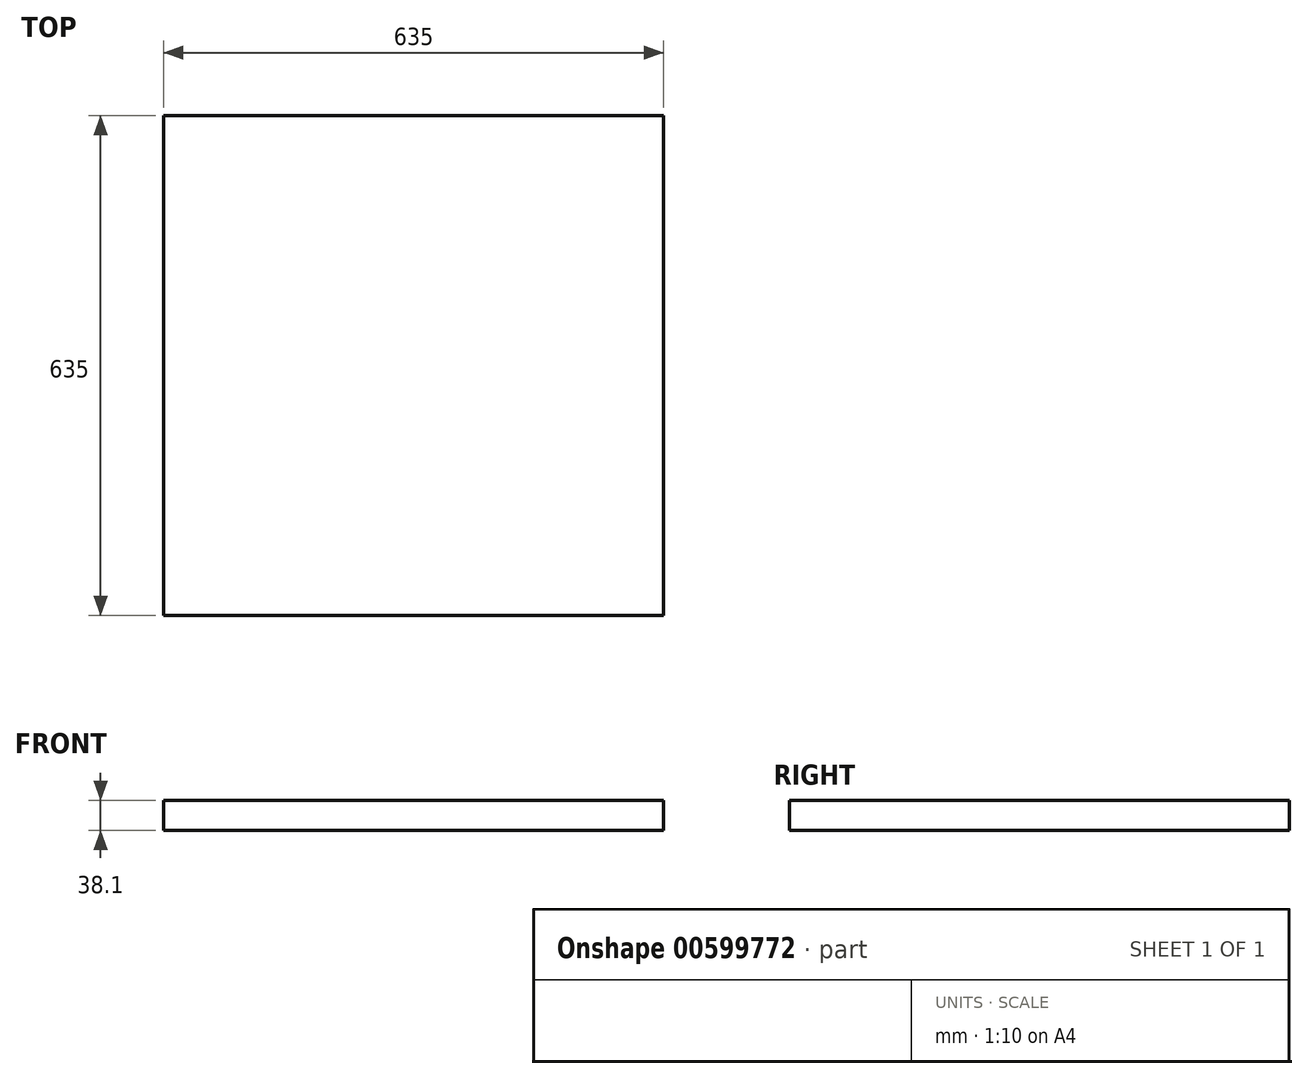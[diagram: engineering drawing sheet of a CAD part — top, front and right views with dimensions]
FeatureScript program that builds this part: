
annotation { "Feature Type Name" : "Feature", "Feature Type Description" : "" }
export const myFeature = defineFeature(function(context is Context, id is Id, definition is map)
    precondition{}
    {
        {
            var Q0;
            Q0=qCreatedBy(makeId("Top.planeOp"),FACE);
            var sketch = newSketch(context, id + "F0", { "sketchPlane" : qUnion([Q0])});
            skLineSegment(sketch, "E0.bottom", {"start": v(317.5, 317.5) * mm, "end": v(-317.5, 317.5) * mm});
            skLineSegment(sketch, "E0.top", {"start": v(317.5, -317.5) * mm, "end": v(-317.5, -317.5) * mm});
            skLineSegment(sketch, "E0.left", {"start": v(317.5, 317.5) * mm, "end": v(317.5, -317.5) * mm});
            skLineSegment(sketch, "E0.right", {"start": v(-317.5, 317.5) * mm, "end": v(-317.5, -317.5) * mm});
            skPoint(sketch, "E0.middle", {"position": v(0, 0) * mm});
            skSolve(sketch);
        }
        {
            var Q0;
            Q0 = qSketchRegion(id + "F0", true);
            extrude(context, id + "F1", {"entities" : qUnion([Q0]), "depth" : 38.1 * mm, "offsetDistance" : 25.4 * mm});
        }
    });
